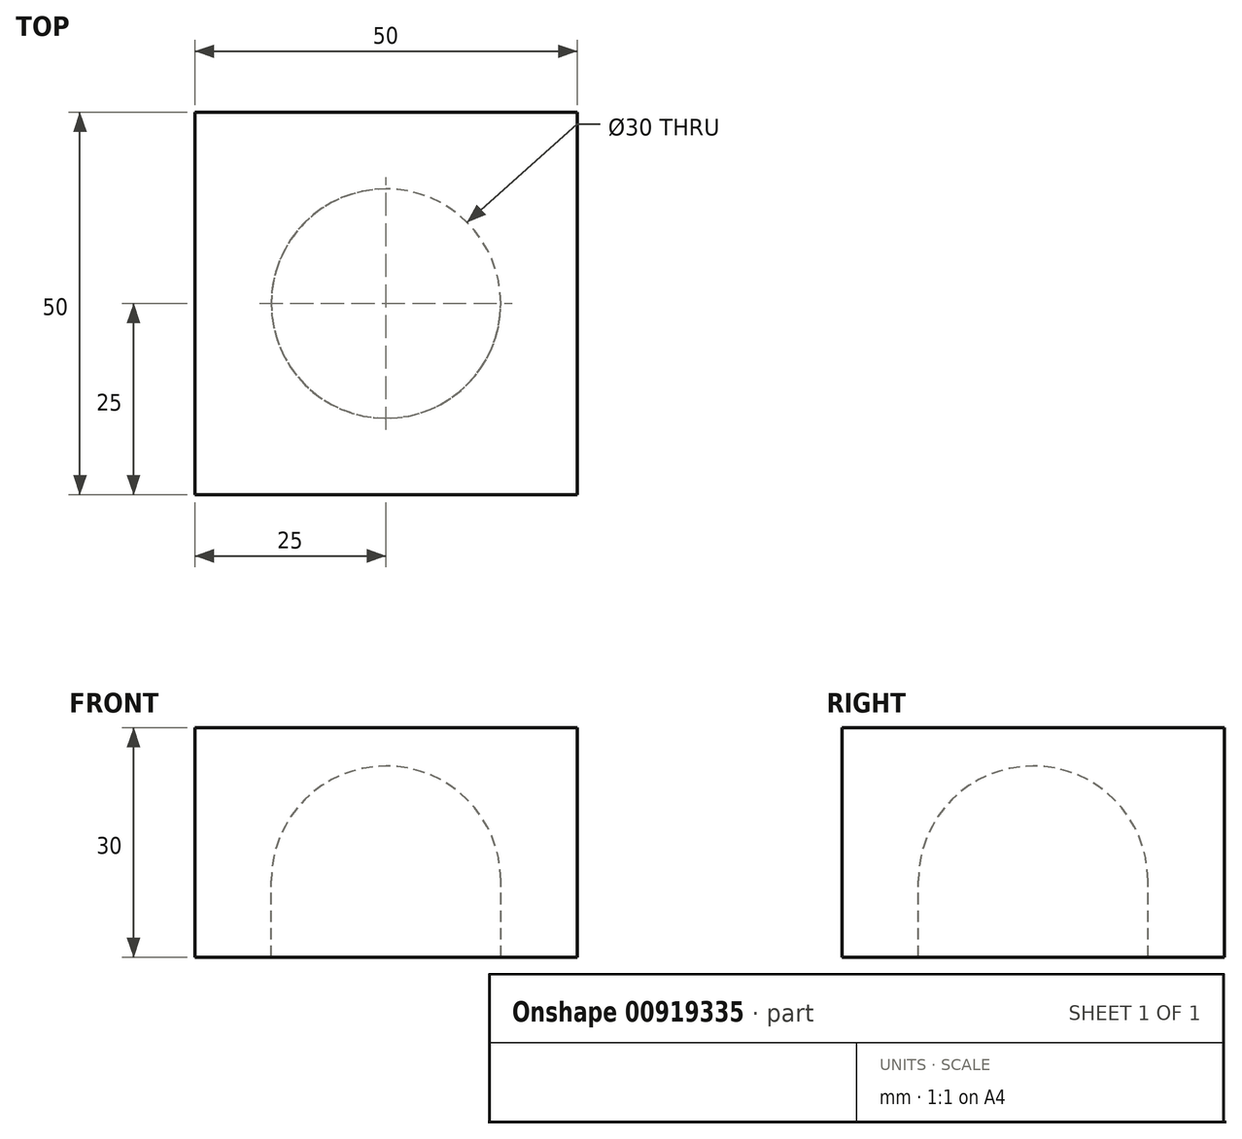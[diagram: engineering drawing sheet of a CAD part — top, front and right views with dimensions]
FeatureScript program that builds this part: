
annotation { "Feature Type Name" : "Feature", "Feature Type Description" : "" }
export const myFeature = defineFeature(function(context is Context, id is Id, definition is map)
    precondition{}
    {
        {
            var Q0;
            Q0=qCreatedBy(makeId("Top.planeOp"),FACE);
            var sketch = newSketch(context, id + "F0", { "sketchPlane" : qUnion([Q0])});
            skLineSegment(sketch, "E0.bottom", {"start": v(0, 0) * mm, "end": v(50, 0) * mm});
            skLineSegment(sketch, "E0.top", {"start": v(0, 50) * mm, "end": v(50, 50) * mm});
            skLineSegment(sketch, "E0.left", {"start": v(0, 0) * mm, "end": v(0, 50) * mm});
            skLineSegment(sketch, "E0.right", {"start": v(50, 0) * mm, "end": v(50, 50) * mm});
            skSolve(sketch);
        }
        {
            var Q0;
            Q0 = qSketchRegion(id + "F0", true);
            extrude(context, id + "F1", {"entities" : qUnion([Q0]), "depth" : 30 * mm, "offsetDistance" : 25 * mm});
        }
        {
            var Q0;
            Q0=makeQuery(id+"F1.opExtrude","CAP_FACE",FACE,{"disambiguationData":[OSD([sQuery(id+"F0.wireOp",EDGE,"E0.bottom"),sQuery(id+"F0.wireOp",EDGE,"E0.top"),sQuery(id+"F0.wireOp",EDGE,"E0.left"),sQuery(id+"F0.wireOp",EDGE,"E0.right")])],"isStart":true});
            var sketch = newSketch(context, id + "F2", { "sketchPlane" : qUnion([Q0])});
            skCircle(sketch, "E1", {"center": v(25, -25) * mm, "radius": 15 * mm});
            skLineSegment(sketch, "E2", {"start": v(25, -10) * mm, "end": v(25, -40) * mm});
            skSolve(sketch);
        }
        {
            var Q0;
            {var subQ0=sQuery(id+"F2.wireOp",EDGE,"E2");Q0=makeQuery(id+"F2.imprint","IMPRINT",FACE,{"disambiguationData":[TD([[makeQuery(id+"F2.imprint","IMPRINT",EDGE,{"derivedFrom":subQ0}),1.0]])]});}
            var Q1;
            Q1=sQuery(id+"F2.wireOp",EDGE,"E2");
            revolve(context, id + "F3", {"operationType" : NewBodyOperationType.REMOVE, "surfaceOperationType" : NewSurfaceOperationType.NEW, "entities" : qUnion([Q0]), "axis" : qUnion([Q1]), "revolveType" : RevolveType.FULL, "oppositeDirection" : true});
        }
        {
            var Q0;
            Q0=makeQuery(id+"F1.opExtrude","CAP_FACE",FACE,{"disambiguationData":[OSD([sQuery(id+"F0.wireOp",EDGE,"E0.bottom"),sQuery(id+"F0.wireOp",EDGE,"E0.top"),sQuery(id+"F0.wireOp",EDGE,"E0.left"),sQuery(id+"F0.wireOp",EDGE,"E0.right")])],"isStart":true});
            var sketch = newSketch(context, id + "F4", { "sketchPlane" : qUnion([Q0])});
            skSolve(sketch);
        }
        {
            var Q0;
            {var subQ3=sQuery(id+"F0.wireOp",EDGE,"E0.bottom");Q0=makeQuery(id+"F4.imprint","IMPRINT",FACE,{"disambiguationData":[TD([[makeQuery(id+"F4.imprint","IMPRINT",EDGE,{"derivedFrom":makeQuery(id+"F1.opExtrude","CAP_EDGE",EDGE,{"disambiguationData":[OSD([subQ3])],"isStart":true})}),-1.0]])]});}
            extrude(context, id + "F5", {"entities" : qUnion([Q0]), "operationType" : NewBodyOperationType.ADD, "depth" : 10 * mm, "offsetDistance" : 25 * mm});
        }
        {
            var Q0;
            Q0=makeQuery(id+"F1.opExtrude","CAP_FACE",FACE,{"disambiguationData":[OSD([sQuery(id+"F0.wireOp",EDGE,"E0.bottom"),sQuery(id+"F0.wireOp",EDGE,"E0.top"),sQuery(id+"F0.wireOp",EDGE,"E0.left"),sQuery(id+"F0.wireOp",EDGE,"E0.right")])],"isStart":false});
            extrude(context, id + "F6", {"entities" : qUnion([Q0]), "operationType" : NewBodyOperationType.REMOVE, "oppositeDirection" : true, "depth" : 10 * mm, "offsetDistance" : 25 * mm});
        }
    });
